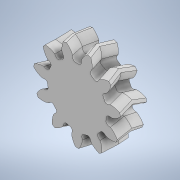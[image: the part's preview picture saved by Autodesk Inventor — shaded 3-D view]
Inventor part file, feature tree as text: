
AUTODESK INVENTOR PART (.ipt)
format: ipt  version: 2022 (Build 260153070, 153G)  size: 530,432 bytes
history: native  units: mm
features: sketch x1, extrude x1, helix x1, pattern_circular x1, mirror x1
ambient origin geometry x8: Origin, YZ Plane, XZ Plane, XY Plane, X Axis, Y Axis, Z Axis, Center Point
bodies: Solid1 (feature_tree)
feature tree (5):
  sketch  "Sketch1"  dims[d0=1.5mm d1=0.0mm d2=93.468379mm d3=1.5mm d4=10.0mm d5=0.0mm d6=90.0deg d7=90.0deg d8=0.0mm d9=0.0mm d10=110.0mm d11=360.0deg]
  extrude  "Extrusion1"  TaperAngle=0.0deg  [1 undecoded]
  helix  "Coil1"  [1 undecoded]
  pattern_circular  "Circular Pattern1"  [2 undecoded]
  mirror  "Mirror1"
note: 4 required parameter values undecoded (feature->parameter linkage not recoverable at this tier; creation-order binding heuristic only, values carry confidence <= 0.55)
